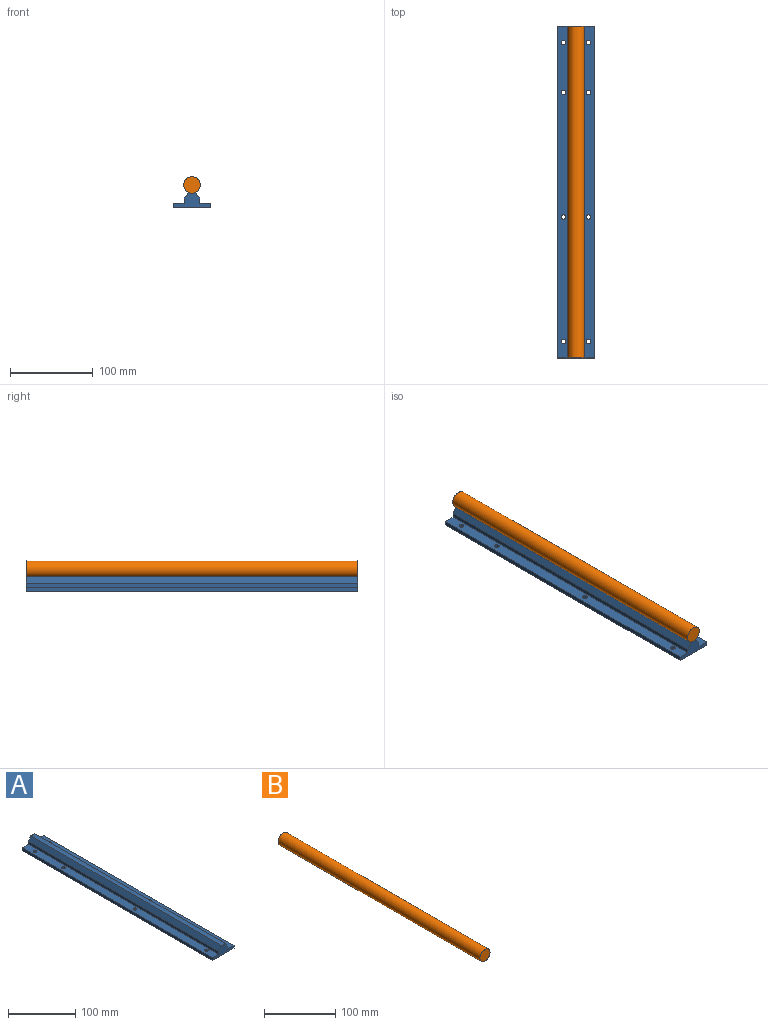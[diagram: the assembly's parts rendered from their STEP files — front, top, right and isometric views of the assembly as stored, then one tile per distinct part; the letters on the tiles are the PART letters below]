
ASSEMBLY  parts=2 mates=1
PART A: 20 faces, bbox 45x400x17.8 mm
  f0: plane 400x7.84mm, normal (-0.82,0,0.57), area 3829mm2, adj f1,f9,f10,f11
  f1: plane 400x5mm, normal (-1,0,0), area 2000mm2, adj f0,f2,f10,f11
  f2: plane 400x13mm, normal (0,0,1), area 5105mm2, adj f1,f3,f10,f11,f12,f14,f16,f18
  f3: plane 400x5mm, normal (-1,0,0), area 2000mm2, adj f2,f4,f10,f11
  f4: plane 400x45mm, normal (0,0,-1), area 17809.9mm2, adj f3,f5,f10,f11,f12,f13,f14,f15
  f5: plane 400x5mm, normal (1,0,0), area 2000mm2, adj f4,f6,f10,f11
  f6: plane 400x13mm, normal (0,0,1), area 5105mm2, adj f5,f7,f10,f11,f13,f15,f17,f19
  f7: plane 400x5mm, normal (1,0,0), area 2000mm2, adj f6,f8,f10,f11
  f8: plane 400x7.84mm, normal (0.82,0,0.57), area 3829mm2, adj f7,f9,f10,f11
  f9: cylinder r=10mm len=400mm, axis (0,-1,0), area 3292.1mm2, adj f0,f8,f10,f11
  f10: plane 45x17.84mm, normal (0,1,0), area 421.3mm2, adj f0,f1,f2,f3,f4,f5,f6,f7
  f11: plane 45x17.84mm, normal (0,-1,0), area 421.3mm2, adj f0,f1,f2,f3,f4,f5,f6,f7
  f12: cylinder r=2.75mm len=5.5mm, axis (0,0,-1), area 86.4mm2, adj f2,f4
  f13: cylinder r=2.75mm len=5.5mm, axis (0,0,-1), area 86.4mm2, adj f4,f6
  f14: cylinder r=2.75mm len=5.5mm, axis (0,0,-1), area 86.4mm2, adj f2,f4
  f15: cylinder r=2.75mm len=5.5mm, axis (0,0,-1), area 86.4mm2, adj f4,f6
  f16: cylinder r=2.75mm len=5.5mm, axis (0,0,-1), area 86.4mm2, adj f2,f4
  f17: cylinder r=2.75mm len=5.5mm, axis (0,0,-1), area 86.4mm2, adj f4,f6
  f18: cylinder r=2.75mm len=5.5mm, axis (0,0,-1), area 86.4mm2, adj f2,f4
  f19: cylinder r=2.75mm len=5.5mm, axis (0,0,-1), area 86.4mm2, adj f4,f6
PART B: 3 faces, bbox 20x400x20 mm
  f0: cylinder r=10mm len=400mm, axis (0,-1,0), area 25132.7mm2, adj f1,f2
  f1: plane 20x20mm, normal (0,1,0), area 314.2mm2, adj f0
  f2: plane 20x20mm, normal (0,-1,0), area 314.2mm2, adj f0
PLACE A t=(44.97,-128.87,90.54)mm
PLACE B t=(44.97,-128.87,90.54)mm
MATE fastened B.f0 <-> A.f9  axis (0,-1,0) through (-12.53,-128.87,117.54)mm
